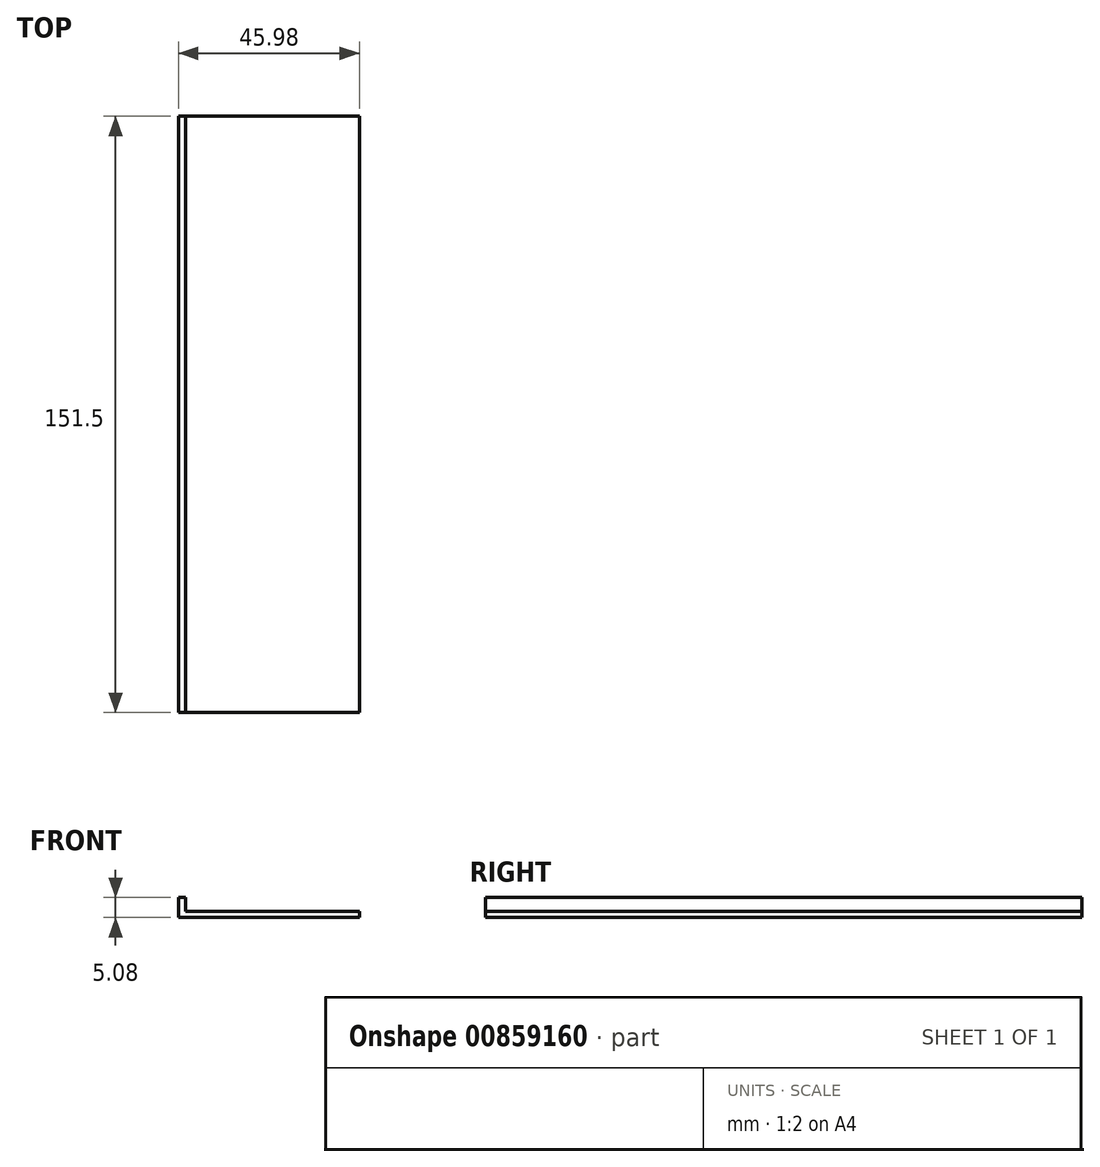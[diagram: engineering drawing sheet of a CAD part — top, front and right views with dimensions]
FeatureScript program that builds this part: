
annotation { "Feature Type Name" : "Feature", "Feature Type Description" : "" }
export const myFeature = defineFeature(function(context is Context, id is Id, definition is map)
    precondition{}
    {
        {
            var Q0;
            Q0=qCreatedBy(makeId("Top.planeOp"),FACE);
            var sketch = newSketch(context, id + "F0", { "sketchPlane" : qUnion([Q0])});
            skLineSegment(sketch, "E0", {"start": v(-55.17, 61.75) * mm, "end": v(-55.17, -89.75) * mm});
            skLineSegment(sketch, "E1", {"start": v(-55.17, -89.75) * mm, "end": v(-9.19, -89.75) * mm});
            skLineSegment(sketch, "E2", {"start": v(-55.17, 61.75) * mm, "end": v(-9.19, 61.75) * mm});
            skLineSegment(sketch, "E3", {"start": v(-9.19, 61.75) * mm, "end": v(-9.19, -89.75) * mm});
            skSolve(sketch);
        }
        {
            var Q0;
            Q0 = qSketchRegion(id + "F0", true);
            extrude(context, id + "F1", {"entities" : qUnion([Q0]), "depth" : 5.08 * mm, "offsetDistance" : 25.4 * mm});
        }
        {
            var Q0;
            Q0=makeQuery(id+"F1.opExtrude","SWEPT_FACE",FACE,{"disambiguationData":[OSD([sQuery(id+"F0.wireOp",EDGE,"E1")])]});
            var sketch = newSketch(context, id + "F2", { "sketchPlane" : qUnion([Q0])});
            skLineSegment(sketch, "E4", {"start": v(-53.38, 5.08) * mm, "end": v(-53.38, 1.53) * mm});
            skLineSegment(sketch, "E5", {"start": v(-53.38, 1.53) * mm, "end": v(-9.19, 1.53) * mm});
            skLineSegment(sketch, "E6", {"start": v(-9.19, 1.53) * mm, "end": v(-9.19, 5.08) * mm});
            skLineSegment(sketch, "E7", {"start": v(-9.19, 5.08) * mm, "end": v(-53.38, 5.08) * mm});
            skSolve(sketch);
        }
        {
            var Q0;
            Q0=makeQuery(id+"F2.imprint","IMPRINT",FACE,{"disambiguationData":[TD([[makeQuery(id+"F2.imprint","IMPRINT",EDGE,{"derivedFrom":sQuery(id+"F2.wireOp",EDGE,"E4")}),1.0]])]});
            extrude(context, id + "F3", {"entities" : qUnion([Q0]), "operationType" : NewBodyOperationType.REMOVE, "endBound" : BoundingType.THROUGH_ALL, "oppositeDirection" : true, "depth" : 25.4 * mm, "offsetDistance" : 25.4 * mm});
        }
    });
